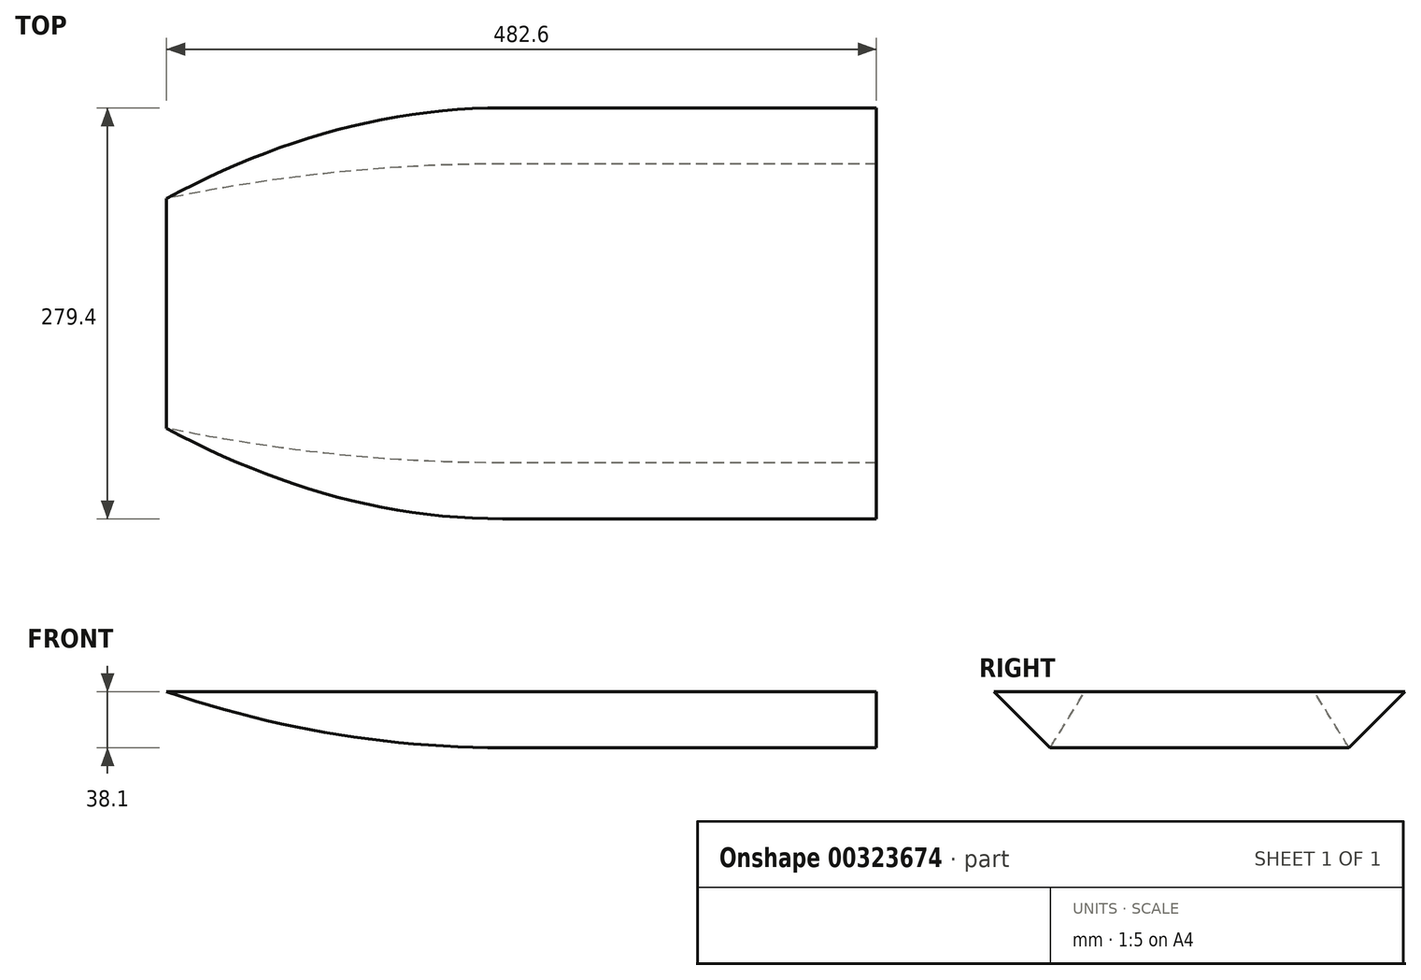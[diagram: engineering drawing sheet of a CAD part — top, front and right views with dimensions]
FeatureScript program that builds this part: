
annotation { "Feature Type Name" : "Feature", "Feature Type Description" : "" }
export const myFeature = defineFeature(function(context is Context, id is Id, definition is map)
    precondition{}
    {
        {
            var Q0;
            Q0=qCreatedBy(makeId("Front.planeOp"),FACE);
            var sketch = newSketch(context, id + "F0", { "sketchPlane" : qUnion([Q0])});
            skLineSegment(sketch, "E0.bottom", {"start": v(0, 0) * mm, "end": v(254, 0) * mm});
            skLineSegment(sketch, "E0.right", {"start": v(254, 0) * mm, "end": v(254, 38.1) * mm});
            skLineSegment(sketch, "E1", {"start": v(254, 38.1) * mm, "end": v(-228.6, 38.1) * mm});
            skArc(sketch, "E2", {"start": v(0, 0) * mm, "mid": v(-115.88, 9.6) * mm, "end": v(-228.6, 38.1) * mm});
            skSolve(sketch);
        }
        {
            var Q0;
            Q0=makeQuery(id+"F0.imprint","IMPRINT",FACE,{"disambiguationData":[TD([[makeQuery(id+"F0.imprint","IMPRINT",EDGE,{"derivedFrom":sQuery(id+"F0.wireOp",EDGE,"E0.bottom")}),1.0]])]});
            extrude(context, id + "F1", {"entities" : qUnion([Q0]), "depth" : 88.9 * mm});
        }
        {
            var Q0;
            Q0=makeQuery(id+"F1.opExtrude","CAP_FACE",FACE,{"disambiguationData":[OSD([sQuery(id+"F0.wireOp",EDGE,"E0.bottom"),sQuery(id+"F0.wireOp",EDGE,"E0.right"),sQuery(id+"F0.wireOp",EDGE,"E1"),sQuery(id+"F0.wireOp",EDGE,"E2")])],"isStart":false});
            extrude(context, id + "F2", {"entities" : qUnion([Q0]), "operationType" : NewBodyOperationType.ADD, "depth" : 50.8 * mm});
        }
        {
            var Q0;
            {var subQ0=sQuery(id+"F0.wireOp",EDGE,"E1");Q0=makeQuery(id+"F2.boolean.opBoolean","MERGE",FACE,{"derivedFrom":[makeQuery(id+"F1.opExtrude","SWEPT_FACE",FACE,{"disambiguationData":[OSD([subQ0])]}),makeQuery(id+"F2.opExtrude","SWEPT_FACE",FACE,{"disambiguationData":[OSD([subQ0])]})]});}
            var sketch = newSketch(context, id + "F3", { "sketchPlane" : qUnion([Q0])});
            skLineSegment(sketch, "E3", {"start": v(-304.42, -139.7) * mm, "end": v(0, -139.7) * mm});
            skArc(sketch, "E4", {"start": v(-228.6, -114.3) * mm, "mid": v(-115, -133.33) * mm, "end": v(0, -139.7) * mm});
            skLineSegment(sketch, "E5", {"start": v(-304.42, -139.7) * mm, "end": v(-304.42, -114.3) * mm});
            skLineSegment(sketch, "E6", {"start": v(-304.42, -114.3) * mm, "end": v(-228.6, -114.3) * mm});
            skSolve(sketch);
        }
        {
            var Q0;
            Q0=qSketchRegion(id+"F3",true);
            extrude(context, id + "F4", {"entities" : qUnion([Q0]), "operationType" : NewBodyOperationType.REMOVE, "endBound" : BoundingType.THROUGH_ALL, "oppositeDirection" : true, "depth" : 25.4 * mm});
        }
        {
            var Q0;
            Q0=makeQuery(id+"F2.opExtrude","CAP_EDGE",EDGE,{"disambiguationData":[OSD([sQuery(id+"F0.wireOp",EDGE,"E0.bottom")])],"isStart":false});
            chamfer(context, id + "F5", {"entities" : qUnion([Q0]), "width" : 38.1 * mm, "tangentPropagation" : true});
        }
        {
            var Q0;
            Q0=makeQuery(id+"F1.opExtrude","SWEPT_BODY",BODY,{"disambiguationData":[OSD([sQuery(id+"F0.wireOp",EDGE,"E0.bottom"),sQuery(id+"F0.wireOp",EDGE,"E0.right"),sQuery(id+"F0.wireOp",EDGE,"E1"),sQuery(id+"F0.wireOp",EDGE,"E2")])]});
            var Q1;
            Q1=qCreatedBy(makeId("Front.planeOp"),FACE);
            mirror(context, id + "F6", {"operationType" : NewBodyOperationType.ADD, "entities" : qUnion([Q0]), "mirrorPlane" : qUnion([Q1])});
        }
    });
